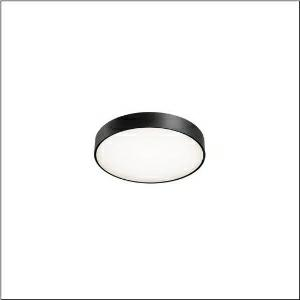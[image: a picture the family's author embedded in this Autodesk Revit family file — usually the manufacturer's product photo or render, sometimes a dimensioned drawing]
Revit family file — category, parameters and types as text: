
# Revit family: round_21_s_51mr34gd0321b
name_source: partatom
category: Lighting Fixtures
units: mm (PartAtom-declared; Revit-internal decimal feet)

## family parameters
Cut with Voids When Loaded = No
Host = Face
Light Source = No
Part Type = Normal
Room Calculation Point = No
Round Connector Dimension = Use Diameter
Shared = No

## types (1)
- Round 21 S (1 x LED, 3930 lm, 28.3 W, 3000K)
    Apparent Load = 28 VA
    CIE Flux Codes = 49 80 96 79 100
    Color Rendering = 80
    Color Temperature = 3000K
    Default Elevation = 1800 mm
    Description = Round 21 S, wall and ceiling luminaire, primary optical cover: cover, of PMMA, opal, light emission: direct/indirect distribution, primary light characteristic: symmetric, installation type: suspended mounting, surface-mounted, LED, rated luminous flux: 3.930lm, luminous efficacy: 139lm/W, light colour: 830, colour temperature: 3000K, control gear: DALI 2, with terminal, 5-pole, mains connection: 230V, AC, 50/60Hz, rated input power: 28.3W, housing, of aluminium, coated, black, diameter: 400mm, height: 62mm, protection rating (complete): IP40, insulation class (complete): insulation class I (protective earthing), certification: CE, impact resistance: IK04, permissible operating ambient temperature: -10..+35°C, packaging unit: 1 piece
    Height = 87 mm
    Lamp = 1 x LED
    Lamp Light Flux = 3930 lm
    Lamp Power = 28.3 W
    Lamp count = 1
    Length = 400 mm
    Luminous efficacy = 139 lm/W
    Manufacturer = Siteco
    ModVariant = No
    Model = 51MR34GD0321B
    Mounting Place = Ceiling
    Mounting Type = Surface mounted
    Number of Poles = 1
    OnlyDefault = Yes
    Power Factor = 1
    Product Name = Round 21 S
    Product group = wall and ceiling luminaire
    ProductGroupID = 304
    Protection Class = Protection class I
    Protection Degree = IP 40
    RLX_Detail_Level = 1
    RLX_Emergency_Light_Flux = 0 lm
    RLX_Emergency_Type = 0
    RLX_Emergency_Type_DB = No
    RlxData = <blob elided: 13869 chars, md5=a6ff5b23>
    Socket = socket
    Standby Power = 0 W
    System Light Flux = 3930 lm
    System Power = 28 W
    Type Comments = Product without accessories
    Type Image = l_1258311.jpg
    URL = http://relux.com
    VarID = ---
    Voltage = 0 V
    Weight = 0.00 kg
    Width = 0 mm  [stored 0 ft]

note: [stored X ft] marks values corroborated as IEEE doubles in the binary element streams (Revit-internal decimal feet)

## geometry (parser evidence)
native form markers: Sweep x16
no freeform markers — native parametric forms only
